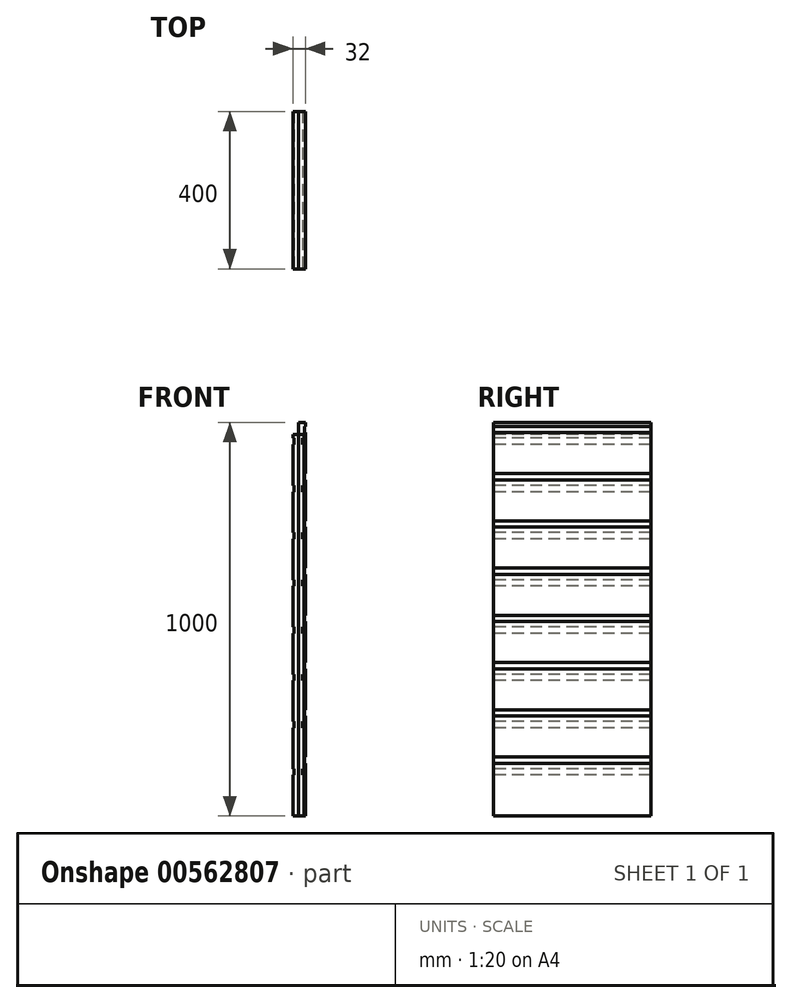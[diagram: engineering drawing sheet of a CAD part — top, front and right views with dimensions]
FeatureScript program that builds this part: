
annotation { "Feature Type Name" : "Feature", "Feature Type Description" : "" }
export const myFeature = defineFeature(function(context is Context, id is Id, definition is map)
    precondition{}
    {
        {
            var Q0;
            Q0=qCreatedBy(makeId("Front.planeOp"),FACE);
            var sketch = newSketch(context, id + "F0", { "sketchPlane" : qUnion([Q0])});
            skLineSegment(sketch, "E0", {"start": v(0, 0) * mm, "end": v(0, 1000) * mm});
            skLineSegment(sketch, "E1", {"start": v(18, 1000) * mm, "end": v(18, 990) * mm});
            skLineSegment(sketch, "E2", {"start": v(18, 990) * mm, "end": v(15, 990) * mm});
            skLineSegment(sketch, "E3", {"start": v(15, 990) * mm, "end": v(15, 974) * mm});
            skLineSegment(sketch, "E4", {"start": v(15, 974) * mm, "end": v(18, 974) * mm});
            skLineSegment(sketch, "E5", {"start": v(18, 974) * mm, "end": v(18, 870) * mm});
            skLineSegment(sketch, "E6", {"start": v(0, 1000) * mm, "end": v(18, 1000) * mm});
            skLineSegment(sketch, "E7.0.1.0", {"start": v(18, 854) * mm, "end": v(18, 750) * mm});
            skLineSegment(sketch, "E7.0.1.1", {"start": v(15, 870) * mm, "end": v(15, 854) * mm});
            skLineSegment(sketch, "E7.0.1.2", {"start": v(15, 854) * mm, "end": v(18, 854) * mm});
            skLineSegment(sketch, "E7.0.1.3", {"start": v(18, 870) * mm, "end": v(15, 870) * mm});
            skLineSegment(sketch, "E7.0.2.0", {"start": v(18, 734) * mm, "end": v(18, 630) * mm});
            skLineSegment(sketch, "E7.0.2.1", {"start": v(15, 750) * mm, "end": v(15, 734) * mm});
            skLineSegment(sketch, "E7.0.2.2", {"start": v(15, 734) * mm, "end": v(18, 734) * mm});
            skLineSegment(sketch, "E7.0.2.3", {"start": v(18, 750) * mm, "end": v(15, 750) * mm});
            skLineSegment(sketch, "E7.0.3.0", {"start": v(18, 614) * mm, "end": v(18, 510) * mm});
            skLineSegment(sketch, "E7.0.3.1", {"start": v(15, 630) * mm, "end": v(15, 614) * mm});
            skLineSegment(sketch, "E7.0.3.2", {"start": v(15, 614) * mm, "end": v(18, 614) * mm});
            skLineSegment(sketch, "E7.0.3.3", {"start": v(18, 630) * mm, "end": v(15, 630) * mm});
            skLineSegment(sketch, "E7.0.4.0", {"start": v(18, 494) * mm, "end": v(18, 390) * mm});
            skLineSegment(sketch, "E7.0.4.1", {"start": v(15, 510) * mm, "end": v(15, 494) * mm});
            skLineSegment(sketch, "E7.0.4.2", {"start": v(15, 494) * mm, "end": v(18, 494) * mm});
            skLineSegment(sketch, "E7.0.4.3", {"start": v(18, 510) * mm, "end": v(15, 510) * mm});
            skLineSegment(sketch, "E7.0.5.0", {"start": v(18, 374) * mm, "end": v(18, 270) * mm});
            skLineSegment(sketch, "E7.0.5.1", {"start": v(15, 390) * mm, "end": v(15, 374) * mm});
            skLineSegment(sketch, "E7.0.5.2", {"start": v(15, 374) * mm, "end": v(18, 374) * mm});
            skLineSegment(sketch, "E7.0.5.3", {"start": v(18, 390) * mm, "end": v(15, 390) * mm});
            skLineSegment(sketch, "E7.0.6.0", {"start": v(18, 254) * mm, "end": v(18, 150) * mm});
            skLineSegment(sketch, "E7.0.6.1", {"start": v(15, 270) * mm, "end": v(15, 254) * mm});
            skLineSegment(sketch, "E7.0.6.2", {"start": v(15, 254) * mm, "end": v(18, 254) * mm});
            skLineSegment(sketch, "E7.0.6.3", {"start": v(18, 270) * mm, "end": v(15, 270) * mm});
            skLineSegment(sketch, "E7.0.7.0", {"start": v(18, 134) * mm, "end": v(18, 30) * mm});
            skLineSegment(sketch, "E7.0.7.1", {"start": v(15, 150) * mm, "end": v(15, 134) * mm});
            skLineSegment(sketch, "E7.0.7.2", {"start": v(15, 134) * mm, "end": v(18, 134) * mm});
            skLineSegment(sketch, "E7.0.7.3", {"start": v(18, 150) * mm, "end": v(15, 150) * mm});
            skLineSegment(sketch, "E7.direction1", {"start": v(18, 870) * mm, "end": v(43, 870) * mm, "construction": true});
            skLineSegment(sketch, "E7.direction2", {"start": v(18, 870) * mm, "end": v(18, 750) * mm, "construction": true});
            skLineSegment(sketch, "E8", {"start": v(0, 0) * mm, "end": v(18, 0) * mm});
            skLineSegment(sketch, "E9", {"start": v(18, 0) * mm, "end": v(18, 30) * mm});
            skSolve(sketch);
        }
        {
            var Q0;
            Q0 = qSketchRegion(id + "F0", true);
            extrude(context, id + "F1", {"entities" : qUnion([Q0]), "oppositeDirection" : true, "depth" : 400 * mm, "offsetDistance" : 25 * mm});
        }
        {
            var Q0;
            Q0=qCreatedBy(makeId("Front.planeOp"),FACE);
            var sketch = newSketch(context, id + "F2", { "sketchPlane" : qUnion([Q0])});
            skLineSegment(sketch, "E10", {"start": v(0, 970) * mm, "end": v(14, 970) * mm});
            skLineSegment(sketch, "E11", {"start": v(14, 970) * mm, "end": v(14, 960) * mm});
            skLineSegment(sketch, "E12", {"start": v(14, 960) * mm, "end": v(11, 960) * mm});
            skLineSegment(sketch, "E13", {"start": v(11, 960) * mm, "end": v(11, 944) * mm});
            skLineSegment(sketch, "E14", {"start": v(11, 944) * mm, "end": v(14, 944) * mm});
            skLineSegment(sketch, "E15", {"start": v(14, 944) * mm, "end": v(14, 840) * mm});
            skLineSegment(sketch, "E16.0.1.0", {"start": v(11, 840) * mm, "end": v(11, 824) * mm});
            skLineSegment(sketch, "E16.0.1.1", {"start": v(14, 824) * mm, "end": v(14, 720) * mm});
            skLineSegment(sketch, "E16.0.1.2", {"start": v(14, 840) * mm, "end": v(11, 840) * mm});
            skLineSegment(sketch, "E16.0.1.3", {"start": v(11, 824) * mm, "end": v(14, 824) * mm});
            skLineSegment(sketch, "E16.0.2.0", {"start": v(11, 720) * mm, "end": v(11, 704) * mm});
            skLineSegment(sketch, "E16.0.2.1", {"start": v(14, 704) * mm, "end": v(14, 600) * mm});
            skLineSegment(sketch, "E16.0.2.2", {"start": v(14, 720) * mm, "end": v(11, 720) * mm});
            skLineSegment(sketch, "E16.0.2.3", {"start": v(11, 704) * mm, "end": v(14, 704) * mm});
            skLineSegment(sketch, "E16.0.3.0", {"start": v(11, 600) * mm, "end": v(11, 584) * mm});
            skLineSegment(sketch, "E16.0.3.1", {"start": v(14, 584) * mm, "end": v(14, 480) * mm});
            skLineSegment(sketch, "E16.0.3.2", {"start": v(14, 600) * mm, "end": v(11, 600) * mm});
            skLineSegment(sketch, "E16.0.3.3", {"start": v(11, 584) * mm, "end": v(14, 584) * mm});
            skLineSegment(sketch, "E16.0.4.0", {"start": v(11, 480) * mm, "end": v(11, 464) * mm});
            skLineSegment(sketch, "E16.0.4.1", {"start": v(14, 464) * mm, "end": v(14, 360) * mm});
            skLineSegment(sketch, "E16.0.4.2", {"start": v(14, 480) * mm, "end": v(11, 480) * mm});
            skLineSegment(sketch, "E16.0.4.3", {"start": v(11, 464) * mm, "end": v(14, 464) * mm});
            skLineSegment(sketch, "E16.0.5.0", {"start": v(11, 360) * mm, "end": v(11, 344) * mm});
            skLineSegment(sketch, "E16.0.5.1", {"start": v(14, 344) * mm, "end": v(14, 240) * mm});
            skLineSegment(sketch, "E16.0.5.2", {"start": v(14, 360) * mm, "end": v(11, 360) * mm});
            skLineSegment(sketch, "E16.0.5.3", {"start": v(11, 344) * mm, "end": v(14, 344) * mm});
            skLineSegment(sketch, "E16.0.6.0", {"start": v(11, 240) * mm, "end": v(11, 224) * mm});
            skLineSegment(sketch, "E16.0.6.1", {"start": v(14, 224) * mm, "end": v(14, 120) * mm});
            skLineSegment(sketch, "E16.0.6.2", {"start": v(14, 240) * mm, "end": v(11, 240) * mm});
            skLineSegment(sketch, "E16.0.6.3", {"start": v(11, 224) * mm, "end": v(14, 224) * mm});
            skLineSegment(sketch, "E16.0.7.0", {"start": v(11, 120) * mm, "end": v(11, 104) * mm});
            skLineSegment(sketch, "E16.0.7.1", {"start": v(14, 104) * mm, "end": v(14, 0) * mm});
            skLineSegment(sketch, "E16.0.7.2", {"start": v(14, 120) * mm, "end": v(11, 120) * mm});
            skLineSegment(sketch, "E16.0.7.3", {"start": v(11, 104) * mm, "end": v(14, 104) * mm});
            skLineSegment(sketch, "E16.direction1", {"start": v(14, 840) * mm, "end": v(39, 840) * mm, "construction": true});
            skLineSegment(sketch, "E16.direction2", {"start": v(14, 840) * mm, "end": v(14, 720) * mm, "construction": true});
            skLineSegment(sketch, "E17", {"start": v(14, 0) * mm, "end": v(0, 0) * mm});
            skLineSegment(sketch, "E18.MirrorCS", {"start": v(-14, 840) * mm, "end": v(-11, 840) * mm});
            skLineSegment(sketch, "E19.MirrorCS", {"start": v(-11, 840) * mm, "end": v(-11, 824) * mm});
            skLineSegment(sketch, "E20.MirrorCS", {"start": v(-11, 824) * mm, "end": v(-14, 824) * mm});
            skLineSegment(sketch, "E21.MirrorCS", {"start": v(-14, 840) * mm, "end": v(-14, 720) * mm, "construction": true});
            skLineSegment(sketch, "E22.MirrorCS", {"start": v(-14, 840) * mm, "end": v(-39, 840) * mm, "construction": true});
            skLineSegment(sketch, "E23.MirrorCS", {"start": v(-11, 344) * mm, "end": v(-14, 344) * mm});
            skLineSegment(sketch, "E24.MirrorCS", {"start": v(-11, 464) * mm, "end": v(-14, 464) * mm});
            skLineSegment(sketch, "E25.MirrorCS", {"start": v(-14, 480) * mm, "end": v(-11, 480) * mm});
            skLineSegment(sketch, "E26.MirrorCS", {"start": v(-11, 360) * mm, "end": v(-11, 344) * mm});
            skLineSegment(sketch, "E27.MirrorCS", {"start": v(-14, 360) * mm, "end": v(-11, 360) * mm});
            skLineSegment(sketch, "E28.MirrorCS", {"start": v(-14, 720) * mm, "end": v(-11, 720) * mm});
            skLineSegment(sketch, "E29.MirrorCS", {"start": v(-14, 464) * mm, "end": v(-14, 360) * mm});
            skLineSegment(sketch, "E30.MirrorCS", {"start": v(-14, 824) * mm, "end": v(-14, 720) * mm});
            skLineSegment(sketch, "E31.MirrorCS", {"start": v(-11, 704) * mm, "end": v(-14, 704) * mm});
            skLineSegment(sketch, "E32.MirrorCS", {"start": v(-11, 224) * mm, "end": v(-14, 224) * mm});
            skLineSegment(sketch, "E33.MirrorCS", {"start": v(-11, 480) * mm, "end": v(-11, 464) * mm});
            skLineSegment(sketch, "E34.MirrorCS", {"start": v(-14, 240) * mm, "end": v(-11, 240) * mm});
            skLineSegment(sketch, "E35.MirrorCS", {"start": v(-14, 600) * mm, "end": v(-11, 600) * mm});
            skLineSegment(sketch, "E36.MirrorCS", {"start": v(-14, 704) * mm, "end": v(-14, 600) * mm});
            skLineSegment(sketch, "E37.MirrorCS", {"start": v(-11, 720) * mm, "end": v(-11, 704) * mm});
            skLineSegment(sketch, "E38.MirrorCS", {"start": v(-11, 944) * mm, "end": v(-14, 944) * mm});
            skLineSegment(sketch, "E39.MirrorCS", {"start": v(-11, 600) * mm, "end": v(-11, 584) * mm});
            skLineSegment(sketch, "E40.MirrorCS", {"start": v(-14, 584) * mm, "end": v(-14, 480) * mm});
            skLineSegment(sketch, "E41.MirrorCS", {"start": v(-14, 960) * mm, "end": v(-11, 960) * mm});
            skLineSegment(sketch, "E42.MirrorCS", {"start": v(-11, 584) * mm, "end": v(-14, 584) * mm});
            skLineSegment(sketch, "E43.MirrorCS", {"start": v(-11, 240) * mm, "end": v(-11, 224) * mm});
            skLineSegment(sketch, "E44.MirrorCS", {"start": v(-14, 120) * mm, "end": v(-11, 120) * mm});
            skLineSegment(sketch, "E45.MirrorCS", {"start": v(-14, 344) * mm, "end": v(-14, 240) * mm});
            skLineSegment(sketch, "E46.MirrorCS", {"start": v(-11, 104) * mm, "end": v(-14, 104) * mm});
            skLineSegment(sketch, "E47.MirrorCS", {"start": v(-14, 944) * mm, "end": v(-14, 840) * mm});
            skLineSegment(sketch, "E48.MirrorCS", {"start": v(-11, 960) * mm, "end": v(-11, 944) * mm});
            skLineSegment(sketch, "E49.MirrorCS", {"start": v(-14, 970) * mm, "end": v(-14, 960) * mm});
            skLineSegment(sketch, "E50.MirrorCS", {"start": v(0, 970) * mm, "end": v(-14, 970) * mm});
            skLineSegment(sketch, "E51.MirrorCS", {"start": v(-14, 224) * mm, "end": v(-14, 120) * mm});
            skLineSegment(sketch, "E52.MirrorCS", {"start": v(-11, 120) * mm, "end": v(-11, 104) * mm});
            skLineSegment(sketch, "E53.MirrorCS", {"start": v(-14, 104) * mm, "end": v(-14, 0) * mm});
            skLineSegment(sketch, "E54.MirrorCS", {"start": v(-14, 0) * mm, "end": v(0, 0) * mm});
            skSolve(sketch);
        }
        {
            var Q0;
            Q0 = qSketchRegion(id + "F2", true);
            extrude(context, id + "F3", {"entities" : qUnion([Q0]), "oppositeDirection" : true, "depth" : 400 * mm, "offsetDistance" : 25 * mm});
        }
    });
